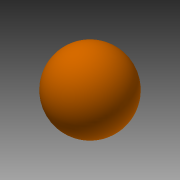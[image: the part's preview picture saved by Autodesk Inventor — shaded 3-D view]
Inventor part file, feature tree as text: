
AUTODESK INVENTOR PART (.ipt)
format: ipt  version: 2015 (Build 190159000, 159)  size: 110,592 bytes
history: native  units: mm
features: revolve x1, sketch x1
ambient origin geometry x8: Origin, YZ Plane, XZ Plane, XY Plane, X Axis, Y Axis, Z Axis, Center Point
bodies: Solid1 (feature_tree)
feature tree (2):
  revolve  "Revolution1"  Angle=180.0deg
  sketch  "Sketch1"  dims[d0=40.0mm d1=180.0deg d2=40.0mm d3=90.0deg]
